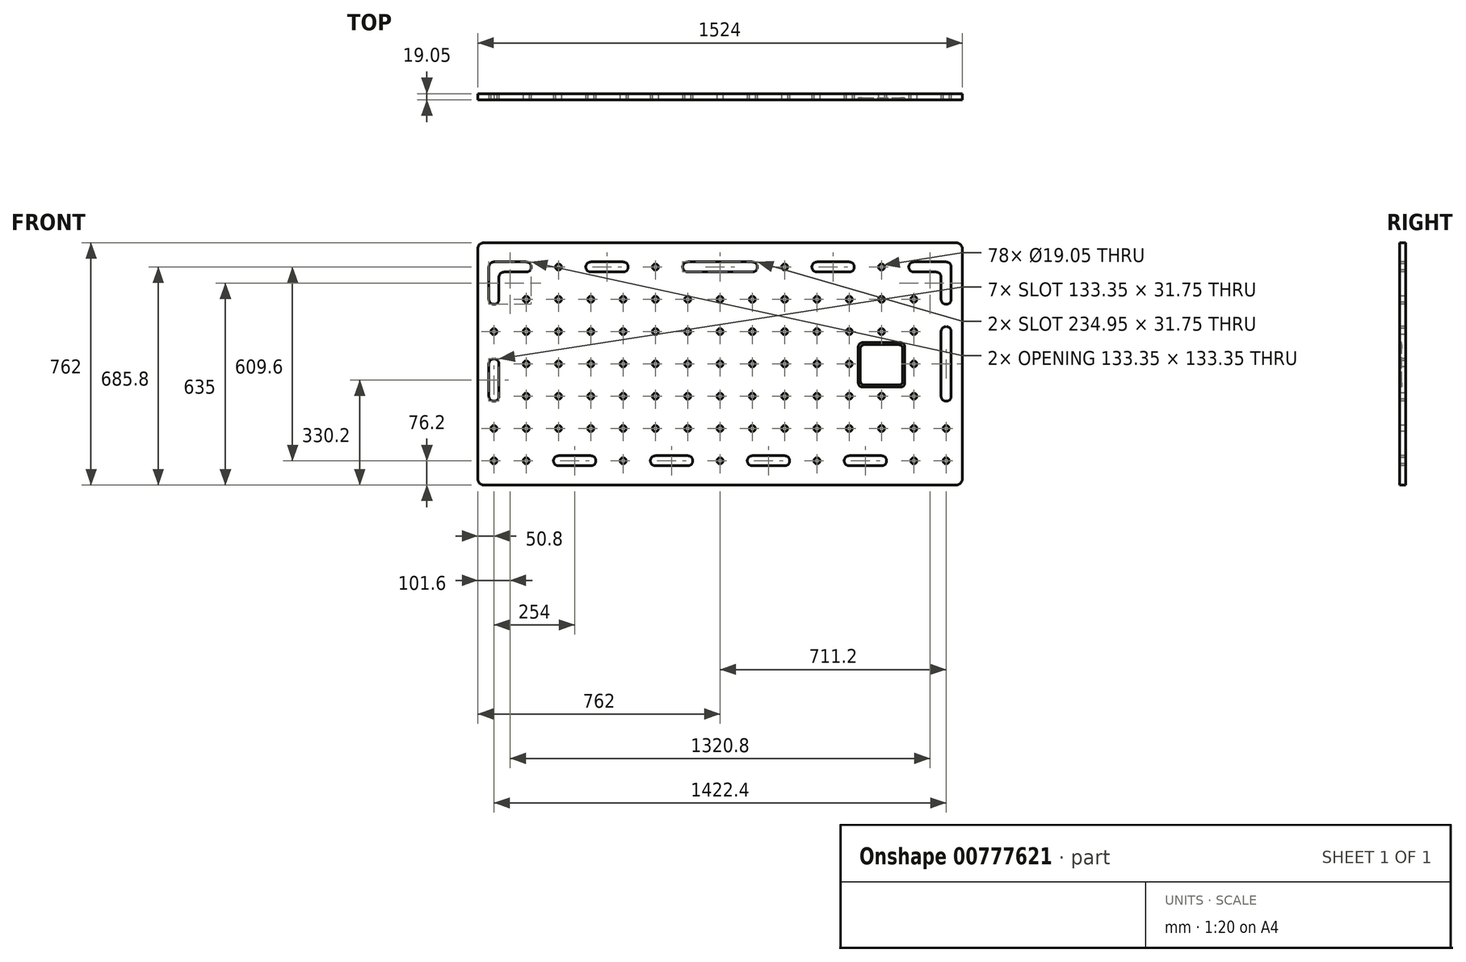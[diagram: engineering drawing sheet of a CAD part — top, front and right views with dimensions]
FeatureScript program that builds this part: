
annotation { "Feature Type Name" : "Feature", "Feature Type Description" : "" }
export const myFeature = defineFeature(function(context is Context, id is Id, definition is map)
    precondition{}
    {
        {
            var Q0;
            Q0=qCreatedBy(makeId("Front.planeOp"),FACE);
            var sketch = newSketch(context, id + "F0", { "sketchPlane" : qUnion([Q0])});
            skLineSegment(sketch, "E0.bottom", {"start": v(742.95, 381) * mm, "end": v(-742.95, 381) * mm});
            skLineSegment(sketch, "E0.top", {"start": v(742.95, -381) * mm, "end": v(-742.95, -381) * mm});
            skLineSegment(sketch, "E0.left", {"start": v(762, 361.95) * mm, "end": v(762, -361.95) * mm});
            skLineSegment(sketch, "E0.right", {"start": v(-762, 361.95) * mm, "end": v(-762, -361.95) * mm});
            skPoint(sketch, "E0.middle", {"position": v(0, 0) * mm});
            skPoint(sketch, "E1.visualSharp", {"position": v(-762, 381) * mm});
            skArc(sketch, "E1.filletArc", {"start": v(-742.95, 381) * mm, "mid": v(-756.42, 375.42) * mm, "end": v(-762, 361.95) * mm});
            skPoint(sketch, "E2.visualSharp", {"position": v(-762, -381) * mm});
            skArc(sketch, "E2.filletArc", {"start": v(-762, -361.95) * mm, "mid": v(-756.42, -375.42) * mm, "end": v(-742.95, -381) * mm});
            skPoint(sketch, "E3.visualSharp", {"position": v(762, -381) * mm});
            skArc(sketch, "E3.filletArc", {"start": v(742.95, -381) * mm, "mid": v(756.42, -375.42) * mm, "end": v(762, -361.95) * mm});
            skPoint(sketch, "E4.visualSharp", {"position": v(762, 381) * mm});
            skArc(sketch, "E4.filletArc", {"start": v(762, 361.95) * mm, "mid": v(756.42, 375.42) * mm, "end": v(742.95, 381) * mm});
            skSolve(sketch);
        }
        {
            var Q0;
            Q0=makeQuery(id+"F0.imprint","IMPRINT",FACE,{"disambiguationData":[TD([[makeQuery(id+"F0.imprint","IMPRINT",EDGE,{"derivedFrom":sQuery(id+"F0.wireOp",EDGE,"E0.bottom")}),1.0]])]});
            extrude(context, id + "F1", {"entities" : qUnion([Q0]), "flatOperationType" : FlatOperationType.REMOVE, "depth" : 19.05 * mm, "offsetDistance" : 25.4 * mm, "domain" : OperationDomain.MODEL});
        }
        {
            var Q0;
            Q0=makeQuery(id+"F1.opExtrude","CAP_FACE",FACE,{"disambiguationData":[OSD([sQuery(id+"F0.wireOp",EDGE,"E0.bottom"),sQuery(id+"F0.wireOp",EDGE,"E0.top"),sQuery(id+"F0.wireOp",EDGE,"E0.left"),sQuery(id+"F0.wireOp",EDGE,"E0.right"),sQuery(id+"F0.wireOp",EDGE,"E1.filletArc"),sQuery(id+"F0.wireOp",EDGE,"E2.filletArc"),sQuery(id+"F0.wireOp",EDGE,"E3.filletArc"),sQuery(id+"F0.wireOp",EDGE,"E4.filletArc")])],"isStart":false});
            var sketch = newSketch(context, id + "F2", { "sketchPlane" : qUnion([Q0]), "disableImprinting" : false});
            skCircle(sketch, "E5", {"center": v(711.2, -304.8) * mm, "radius": 9.53 * mm});
            skCircle(sketch, "E6.0.1.0", {"center": v(711.2, -203.2) * mm, "radius": 9.53 * mm});
            skCircle(sketch, "E6.1.0.0", {"center": v(609.6, -304.8) * mm, "radius": 9.53 * mm});
            skCircle(sketch, "E6.1.1.0", {"center": v(609.6, -203.2) * mm, "radius": 9.53 * mm});
            skCircle(sketch, "E6.1.2.0", {"center": v(609.6, -101.6) * mm, "radius": 9.53 * mm});
            skCircle(sketch, "E6.1.3.0", {"center": v(609.6, 0) * mm, "radius": 9.53 * mm});
            skCircle(sketch, "E6.1.4.0", {"center": v(609.6, 101.6) * mm, "radius": 9.53 * mm});
            skCircle(sketch, "E6.1.5.0", {"center": v(609.6, 203.2) * mm, "radius": 9.53 * mm});
            skCircle(sketch, "E6.2.1.0", {"center": v(508, -203.2) * mm, "radius": 9.53 * mm});
            skCircle(sketch, "E6.2.2.0", {"center": v(508, -101.6) * mm, "radius": 9.53 * mm});
            skCircle(sketch, "E6.2.4.0", {"center": v(508, 101.6) * mm, "radius": 9.53 * mm});
            skCircle(sketch, "E6.2.5.0", {"center": v(508, 203.2) * mm, "radius": 9.53 * mm});
            skCircle(sketch, "E6.2.6.0", {"center": v(508, 304.8) * mm, "radius": 9.53 * mm});
            skCircle(sketch, "E6.3.1.0", {"center": v(406.4, -203.2) * mm, "radius": 9.53 * mm});
            skCircle(sketch, "E6.3.2.0", {"center": v(406.4, -101.6) * mm, "radius": 9.53 * mm});
            skCircle(sketch, "E6.3.3.0", {"center": v(406.4, 0) * mm, "radius": 9.53 * mm});
            skCircle(sketch, "E6.3.4.0", {"center": v(406.4, 101.6) * mm, "radius": 9.53 * mm});
            skCircle(sketch, "E6.3.5.0", {"center": v(406.4, 203.2) * mm, "radius": 9.53 * mm});
            skCircle(sketch, "E6.4.0.0", {"center": v(304.8, -304.8) * mm, "radius": 9.53 * mm});
            skCircle(sketch, "E6.4.1.0", {"center": v(304.8, -203.2) * mm, "radius": 9.53 * mm});
            skCircle(sketch, "E6.4.2.0", {"center": v(304.8, -101.6) * mm, "radius": 9.53 * mm});
            skCircle(sketch, "E6.4.3.0", {"center": v(304.8, 0) * mm, "radius": 9.53 * mm});
            skCircle(sketch, "E6.4.4.0", {"center": v(304.8, 101.6) * mm, "radius": 9.53 * mm});
            skCircle(sketch, "E6.4.5.0", {"center": v(304.8, 203.2) * mm, "radius": 9.53 * mm});
            skCircle(sketch, "E6.5.1.0", {"center": v(203.2, -203.2) * mm, "radius": 9.53 * mm});
            skCircle(sketch, "E6.5.2.0", {"center": v(203.2, -101.6) * mm, "radius": 9.53 * mm});
            skCircle(sketch, "E6.5.3.0", {"center": v(203.2, 0) * mm, "radius": 9.53 * mm});
            skCircle(sketch, "E6.5.4.0", {"center": v(203.2, 101.6) * mm, "radius": 9.53 * mm});
            skCircle(sketch, "E6.5.5.0", {"center": v(203.2, 203.2) * mm, "radius": 9.53 * mm});
            skCircle(sketch, "E6.5.6.0", {"center": v(203.2, 304.8) * mm, "radius": 9.53 * mm});
            skCircle(sketch, "E6.6.1.0", {"center": v(101.6, -203.2) * mm, "radius": 9.53 * mm});
            skCircle(sketch, "E6.6.2.0", {"center": v(101.6, -101.6) * mm, "radius": 9.53 * mm});
            skCircle(sketch, "E6.6.3.0", {"center": v(101.6, 0) * mm, "radius": 9.53 * mm});
            skCircle(sketch, "E6.6.4.0", {"center": v(101.6, 101.6) * mm, "radius": 9.53 * mm});
            skCircle(sketch, "E6.6.5.0", {"center": v(101.6, 203.2) * mm, "radius": 9.53 * mm});
            skCircle(sketch, "E6.7.0.0", {"center": v(0, -304.8) * mm, "radius": 9.53 * mm});
            skCircle(sketch, "E6.7.1.0", {"center": v(0, -203.2) * mm, "radius": 9.53 * mm});
            skCircle(sketch, "E6.7.2.0", {"center": v(0, -101.6) * mm, "radius": 9.53 * mm});
            skCircle(sketch, "E6.7.3.0", {"center": v(0, 0) * mm, "radius": 9.53 * mm});
            skCircle(sketch, "E6.7.4.0", {"center": v(0, 101.6) * mm, "radius": 9.53 * mm});
            skCircle(sketch, "E6.7.5.0", {"center": v(0, 203.2) * mm, "radius": 9.53 * mm});
            skCircle(sketch, "E6.8.1.0", {"center": v(-101.6, -203.2) * mm, "radius": 9.53 * mm});
            skCircle(sketch, "E6.8.2.0", {"center": v(-101.6, -101.6) * mm, "radius": 9.53 * mm});
            skCircle(sketch, "E6.8.3.0", {"center": v(-101.6, 0) * mm, "radius": 9.53 * mm});
            skCircle(sketch, "E6.8.4.0", {"center": v(-101.6, 101.6) * mm, "radius": 9.53 * mm});
            skCircle(sketch, "E6.8.5.0", {"center": v(-101.6, 203.2) * mm, "radius": 9.53 * mm});
            skCircle(sketch, "E6.9.1.0", {"center": v(-203.2, -203.2) * mm, "radius": 9.53 * mm});
            skCircle(sketch, "E6.9.2.0", {"center": v(-203.2, -101.6) * mm, "radius": 9.53 * mm});
            skCircle(sketch, "E6.9.3.0", {"center": v(-203.2, 0) * mm, "radius": 9.53 * mm});
            skCircle(sketch, "E6.9.4.0", {"center": v(-203.2, 101.6) * mm, "radius": 9.53 * mm});
            skCircle(sketch, "E6.9.5.0", {"center": v(-203.2, 203.2) * mm, "radius": 9.53 * mm});
            skCircle(sketch, "E6.9.6.0", {"center": v(-203.2, 304.8) * mm, "radius": 9.53 * mm});
            skCircle(sketch, "E6.10.0.0", {"center": v(-304.8, -304.8) * mm, "radius": 9.53 * mm});
            skCircle(sketch, "E6.10.1.0", {"center": v(-304.8, -203.2) * mm, "radius": 9.53 * mm});
            skCircle(sketch, "E6.10.2.0", {"center": v(-304.8, -101.6) * mm, "radius": 9.53 * mm});
            skCircle(sketch, "E6.10.3.0", {"center": v(-304.8, 0) * mm, "radius": 9.53 * mm});
            skCircle(sketch, "E6.10.4.0", {"center": v(-304.8, 101.6) * mm, "radius": 9.53 * mm});
            skCircle(sketch, "E6.10.5.0", {"center": v(-304.8, 203.2) * mm, "radius": 9.53 * mm});
            skCircle(sketch, "E6.11.1.0", {"center": v(-406.4, -203.2) * mm, "radius": 9.53 * mm});
            skCircle(sketch, "E6.11.2.0", {"center": v(-406.4, -101.6) * mm, "radius": 9.53 * mm});
            skCircle(sketch, "E6.11.3.0", {"center": v(-406.4, 0) * mm, "radius": 9.53 * mm});
            skCircle(sketch, "E6.11.4.0", {"center": v(-406.4, 101.6) * mm, "radius": 9.53 * mm});
            skCircle(sketch, "E6.11.5.0", {"center": v(-406.4, 203.2) * mm, "radius": 9.53 * mm});
            skCircle(sketch, "E6.12.1.0", {"center": v(-508, -203.2) * mm, "radius": 9.53 * mm});
            skCircle(sketch, "E6.12.2.0", {"center": v(-508, -101.6) * mm, "radius": 9.53 * mm});
            skCircle(sketch, "E6.12.3.0", {"center": v(-508, 0) * mm, "radius": 9.53 * mm});
            skCircle(sketch, "E6.12.4.0", {"center": v(-508, 101.6) * mm, "radius": 9.53 * mm});
            skCircle(sketch, "E6.12.5.0", {"center": v(-508, 203.2) * mm, "radius": 9.53 * mm});
            skCircle(sketch, "E6.12.6.0", {"center": v(-508, 304.8) * mm, "radius": 9.53 * mm});
            skCircle(sketch, "E6.13.0.0", {"center": v(-609.6, -304.8) * mm, "radius": 9.53 * mm});
            skCircle(sketch, "E6.13.1.0", {"center": v(-609.6, -203.2) * mm, "radius": 9.53 * mm});
            skCircle(sketch, "E6.13.2.0", {"center": v(-609.6, -101.6) * mm, "radius": 9.53 * mm});
            skCircle(sketch, "E6.13.3.0", {"center": v(-609.6, 0) * mm, "radius": 9.53 * mm});
            skCircle(sketch, "E6.13.4.0", {"center": v(-609.6, 101.6) * mm, "radius": 9.53 * mm});
            skCircle(sketch, "E6.13.5.0", {"center": v(-609.6, 203.2) * mm, "radius": 9.53 * mm});
            skCircle(sketch, "E6.14.0.0", {"center": v(-711.2, -304.8) * mm, "radius": 9.53 * mm});
            skCircle(sketch, "E6.14.1.0", {"center": v(-711.2, -203.2) * mm, "radius": 9.53 * mm});
            skCircle(sketch, "E6.14.4.0", {"center": v(-711.2, 101.6) * mm, "radius": 9.53 * mm});
            skLineSegment(sketch, "E7.bottom", {"start": v(447.75, -72.95) * mm, "end": v(568.4, -72.95) * mm});
            skLineSegment(sketch, "E7.top", {"start": v(447.75, 66.75) * mm, "end": v(568.4, 66.75) * mm});
            skLineSegment(sketch, "E7.left", {"start": v(435.05, -60.25) * mm, "end": v(435.05, 54.05) * mm});
            skLineSegment(sketch, "E7.right", {"start": v(581.1, -60.25) * mm, "end": v(581.1, 54.05) * mm});
            skArc(sketch, "E8.filletArc", {"start": v(447.75, 66.75) * mm, "mid": v(438.76, 63.03) * mm, "end": v(435.05, 54.05) * mm});
            skArc(sketch, "E9.filletArc", {"start": v(581.1, 54.05) * mm, "mid": v(577.38, 63.03) * mm, "end": v(568.4, 66.75) * mm});
            skArc(sketch, "E10.filletArc", {"start": v(568.4, -72.95) * mm, "mid": v(577.38, -69.24) * mm, "end": v(581.1, -60.25) * mm});
            skArc(sketch, "E11.filletArc", {"start": v(435.05, -60.25) * mm, "mid": v(438.76, -69.24) * mm, "end": v(447.75, -72.95) * mm});
            skLineSegment(sketch, "E12.0", {"start": v(454.1, 60.4) * mm, "end": v(562.05, 60.4) * mm});
            skLineSegment(sketch, "E12.1", {"start": v(441.4, -53.9) * mm, "end": v(441.4, 47.7) * mm});
            skLineSegment(sketch, "E12.2", {"start": v(454.1, -66.6) * mm, "end": v(562.05, -66.6) * mm});
            skLineSegment(sketch, "E12.3", {"start": v(574.75, -53.9) * mm, "end": v(574.75, 47.7) * mm});
            skArc(sketch, "E13.filletArc", {"start": v(574.75, 47.7) * mm, "mid": v(571.03, 56.68) * mm, "end": v(562.05, 60.4) * mm});
            skArc(sketch, "E14.filletArc", {"start": v(562.05, -66.6) * mm, "mid": v(571.03, -62.89) * mm, "end": v(574.75, -53.9) * mm});
            skArc(sketch, "E15.filletArc", {"start": v(441.4, -53.9) * mm, "mid": v(445.11, -62.89) * mm, "end": v(454.1, -66.6) * mm});
            skArc(sketch, "E16.filletArc", {"start": v(454.1, 60.4) * mm, "mid": v(445.11, 56.68) * mm, "end": v(441.4, 47.7) * mm});
            skLineSegment(sketch, "E17", {"start": v(-775.52, 0) * mm, "end": v(799.36, 0) * mm, "construction": true});
            skArc(sketch, "E18", {"start": v(-508, -288.92) * mm, "mid": v(-523.88, -304.8) * mm, "end": v(-508, -320.67) * mm});
            skArc(sketch, "E19", {"start": v(-406.4, -320.67) * mm, "mid": v(-390.53, -304.8) * mm, "end": v(-406.4, -288.92) * mm});
            skLineSegment(sketch, "E20", {"start": v(-508, -288.92) * mm, "end": v(-406.4, -288.92) * mm});
            skLineSegment(sketch, "E21", {"start": v(-406.4, -320.67) * mm, "end": v(-508, -320.67) * mm});
            skArc(sketch, "E22", {"start": v(-203.2, -288.92) * mm, "mid": v(-219.08, -304.8) * mm, "end": v(-203.2, -320.67) * mm});
            skArc(sketch, "E23", {"start": v(-101.6, -320.67) * mm, "mid": v(-85.73, -304.8) * mm, "end": v(-101.6, -288.92) * mm});
            skLineSegment(sketch, "E24", {"start": v(-203.2, -288.92) * mm, "end": v(-101.6, -288.92) * mm});
            skLineSegment(sketch, "E25", {"start": v(-101.6, -320.67) * mm, "end": v(-203.2, -320.67) * mm});
            skArc(sketch, "E26", {"start": v(-727.08, -101.6) * mm, "mid": v(-711.2, -117.48) * mm, "end": v(-695.33, -101.6) * mm});
            skArc(sketch, "E27", {"start": v(-695.33, 0) * mm, "mid": v(-711.2, 15.87) * mm, "end": v(-727.08, 0) * mm});
            skLineSegment(sketch, "E28", {"start": v(-695.33, 0) * mm, "end": v(-695.33, -101.6) * mm});
            skLineSegment(sketch, "E29", {"start": v(-727.08, 0) * mm, "end": v(-727.08, -101.6) * mm});
            skArc(sketch, "E30", {"start": v(-727.08, 203.2) * mm, "mid": v(-711.2, 187.32) * mm, "end": v(-695.33, 203.2) * mm});
            skArc(sketch, "E31", {"start": v(-711.04, 320.67) * mm, "mid": v(-722.37, 316.08) * mm, "end": v(-727.08, 304.8) * mm});
            skArc(sketch, "E32", {"start": v(-609.6, 288.92) * mm, "mid": v(-593.73, 304.8) * mm, "end": v(-609.6, 320.67) * mm});
            skLineSegment(sketch, "E33", {"start": v(-711.04, 320.67) * mm, "end": v(-609.6, 320.67) * mm});
            skLineSegment(sketch, "E34", {"start": v(-679.45, 288.92) * mm, "end": v(-609.6, 288.92) * mm});
            skLineSegment(sketch, "E35", {"start": v(-695.33, 273.05) * mm, "end": v(-695.33, 203.2) * mm});
            skLineSegment(sketch, "E36", {"start": v(-727.08, 203.2) * mm, "end": v(-727.08, 304.8) * mm});
            skArc(sketch, "E37", {"start": v(-101.6, 320.67) * mm, "mid": v(-117.48, 304.8) * mm, "end": v(-101.6, 288.92) * mm});
            skArc(sketch, "E38", {"start": v(101.6, 288.92) * mm, "mid": v(117.48, 304.8) * mm, "end": v(101.6, 320.67) * mm});
            skLineSegment(sketch, "E39", {"start": v(-101.6, 320.67) * mm, "end": v(101.6, 320.67) * mm});
            skLineSegment(sketch, "E40", {"start": v(101.6, 288.92) * mm, "end": v(-101.6, 288.92) * mm});
            skArc(sketch, "E41", {"start": v(-406.4, 320.67) * mm, "mid": v(-422.28, 304.8) * mm, "end": v(-406.4, 288.92) * mm});
            skArc(sketch, "E42", {"start": v(-304.8, 288.92) * mm, "mid": v(-288.93, 304.8) * mm, "end": v(-304.8, 320.67) * mm});
            skLineSegment(sketch, "E43", {"start": v(-406.4, 320.67) * mm, "end": v(-304.8, 320.67) * mm});
            skLineSegment(sketch, "E44", {"start": v(-406.4, 288.92) * mm, "end": v(-304.8, 288.92) * mm});
            skArc(sketch, "E45", {"start": v(727.08, 101.6) * mm, "mid": v(711.2, 117.47) * mm, "end": v(695.33, 101.6) * mm});
            skArc(sketch, "E46", {"start": v(695.33, -101.6) * mm, "mid": v(711.2, -117.48) * mm, "end": v(727.08, -101.6) * mm});
            skLineSegment(sketch, "E47", {"start": v(727.08, 101.6) * mm, "end": v(727.08, -101.6) * mm});
            skLineSegment(sketch, "E48", {"start": v(695.33, -101.6) * mm, "end": v(695.33, 101.6) * mm});
            skArc(sketch, "E49", {"start": v(101.6, -288.92) * mm, "mid": v(85.73, -304.8) * mm, "end": v(101.6, -320.67) * mm});
            skArc(sketch, "E50", {"start": v(203.2, -320.67) * mm, "mid": v(219.08, -304.8) * mm, "end": v(203.2, -288.92) * mm});
            skLineSegment(sketch, "E51", {"start": v(101.6, -288.92) * mm, "end": v(203.2, -288.92) * mm});
            skLineSegment(sketch, "E52", {"start": v(203.2, -320.67) * mm, "end": v(101.6, -320.67) * mm});
            skArc(sketch, "E53", {"start": v(508, -320.67) * mm, "mid": v(523.88, -304.8) * mm, "end": v(508, -288.92) * mm});
            skArc(sketch, "E54", {"start": v(406.4, -288.92) * mm, "mid": v(390.53, -304.8) * mm, "end": v(406.4, -320.67) * mm});
            skLineSegment(sketch, "E55", {"start": v(406.4, -320.67) * mm, "end": v(508, -320.67) * mm});
            skLineSegment(sketch, "E56", {"start": v(508, -288.92) * mm, "end": v(406.4, -288.92) * mm});
            skPoint(sketch, "E57.visualSharp", {"position": v(-695.33, 288.92) * mm});
            skArc(sketch, "E57.filletArc", {"start": v(-679.45, 288.92) * mm, "mid": v(-690.68, 284.28) * mm, "end": v(-695.33, 273.05) * mm});
            skArc(sketch, "E58", {"start": v(304.8, 320.67) * mm, "mid": v(288.93, 304.8) * mm, "end": v(304.8, 288.92) * mm});
            skArc(sketch, "E59", {"start": v(406.4, 288.92) * mm, "mid": v(422.28, 304.8) * mm, "end": v(406.4, 320.67) * mm});
            skLineSegment(sketch, "E60", {"start": v(304.8, 288.92) * mm, "end": v(406.4, 288.92) * mm});
            skLineSegment(sketch, "E61", {"start": v(406.4, 320.67) * mm, "end": v(304.8, 320.67) * mm});
            skArc(sketch, "E62", {"start": v(609.6, 320.67) * mm, "mid": v(593.73, 304.8) * mm, "end": v(609.6, 288.92) * mm});
            skArc(sketch, "E63", {"start": v(727.08, 304.8) * mm, "mid": v(722.43, 316.03) * mm, "end": v(711.2, 320.67) * mm});
            skArc(sketch, "E64", {"start": v(695.33, 203.2) * mm, "mid": v(711.2, 187.32) * mm, "end": v(727.08, 203.2) * mm});
            skLineSegment(sketch, "E65", {"start": v(609.6, 288.92) * mm, "end": v(679.45, 288.92) * mm});
            skLineSegment(sketch, "E66", {"start": v(711.2, 320.67) * mm, "end": v(609.6, 320.67) * mm});
            skLineSegment(sketch, "E67", {"start": v(695.33, 203.2) * mm, "end": v(695.33, 273.05) * mm});
            skLineSegment(sketch, "E68", {"start": v(727.08, 304.8) * mm, "end": v(727.08, 203.2) * mm});
            skArc(sketch, "E69.filletArc", {"start": v(695.33, 273.05) * mm, "mid": v(690.68, 284.28) * mm, "end": v(679.45, 288.92) * mm});
            skSolve(sketch);
        }
        {
            var Q0;
            Q0=makeQuery(id+"F2.imprint","IMPRINT",FACE,{"disambiguationData":[TD([[makeQuery(id+"F2.imprint","IMPRINT",EDGE,{"derivedFrom":sQuery(id+"F2.wireOp",EDGE,"E7.bottom")}),1.0]])]});
            extrude(context, id + "F3", {"entities" : qUnion([Q0]), "operationType" : NewBodyOperationType.REMOVE, "oppositeDirection" : true, "depth" : 6.35 * mm, "offsetDistance" : 25.4 * mm});
        }
        {
            var Q0;
            Q0=makeQuery(id+"F2.imprint","IMPRINT",FACE,{"disambiguationData":[TD([[makeQuery(id+"F2.imprint","IMPRINT",EDGE,{"derivedFrom":sQuery(id+"F2.wireOp",EDGE,"E6.14.6.0")}),1.0]])]});
            var Q1;
            Q1=makeQuery(id+"F2.imprint","IMPRINT",FACE,{"disambiguationData":[TD([[makeQuery(id+"F2.imprint","IMPRINT",EDGE,{"derivedFrom":sQuery(id+"F2.wireOp",EDGE,"E6.13.6.0")}),1.0]])]});
            var Q2;
            Q2=makeQuery(id+"F2.imprint","IMPRINT",FACE,{"disambiguationData":[TD([[makeQuery(id+"F2.imprint","IMPRINT",EDGE,{"derivedFrom":sQuery(id+"F2.wireOp",EDGE,"E6.12.6.0")}),1.0]])]});
            var Q3;
            Q3=makeQuery(id+"F2.imprint","IMPRINT",FACE,{"disambiguationData":[TD([[makeQuery(id+"F2.imprint","IMPRINT",EDGE,{"derivedFrom":sQuery(id+"F2.wireOp",EDGE,"E6.12.5.0")}),1.0]])]});
            var Q4;
            Q4=makeQuery(id+"F2.imprint","IMPRINT",FACE,{"disambiguationData":[TD([[makeQuery(id+"F2.imprint","IMPRINT",EDGE,{"derivedFrom":sQuery(id+"F2.wireOp",EDGE,"E6.13.5.0")}),1.0]])]});
            var Q5;
            Q5=makeQuery(id+"F2.imprint","IMPRINT",FACE,{"disambiguationData":[TD([[makeQuery(id+"F2.imprint","IMPRINT",EDGE,{"derivedFrom":sQuery(id+"F2.wireOp",EDGE,"E6.14.5.0")}),1.0]])]});
            var Q6;
            Q6=makeQuery(id+"F2.imprint","IMPRINT",FACE,{"disambiguationData":[TD([[makeQuery(id+"F2.imprint","IMPRINT",EDGE,{"derivedFrom":sQuery(id+"F2.wireOp",EDGE,"E6.14.4.0")}),1.0]])]});
            var Q7;
            Q7=makeQuery(id+"F2.imprint","IMPRINT",FACE,{"disambiguationData":[TD([[makeQuery(id+"F2.imprint","IMPRINT",EDGE,{"derivedFrom":sQuery(id+"F2.wireOp",EDGE,"E6.13.4.0")}),1.0]])]});
            var Q8;
            Q8=makeQuery(id+"F2.imprint","IMPRINT",FACE,{"disambiguationData":[TD([[makeQuery(id+"F2.imprint","IMPRINT",EDGE,{"derivedFrom":sQuery(id+"F2.wireOp",EDGE,"E6.12.4.0")}),1.0]])]});
            var Q9;
            Q9=makeQuery(id+"F2.imprint","IMPRINT",FACE,{"disambiguationData":[TD([[makeQuery(id+"F2.imprint","IMPRINT",EDGE,{"derivedFrom":sQuery(id+"F2.wireOp",EDGE,"E6.12.3.0")}),1.0]])]});
            var Q10;
            Q10=makeQuery(id+"F2.imprint","IMPRINT",FACE,{"disambiguationData":[TD([[makeQuery(id+"F2.imprint","IMPRINT",EDGE,{"derivedFrom":sQuery(id+"F2.wireOp",EDGE,"E6.13.3.0")}),1.0]])]});
            var Q11;
            Q11=makeQuery(id+"F2.imprint","IMPRINT",FACE,{"disambiguationData":[TD([[makeQuery(id+"F2.imprint","IMPRINT",EDGE,{"derivedFrom":sQuery(id+"F2.wireOp",EDGE,"E6.14.3.0")}),1.0]])]});
            var Q12;
            Q12=makeQuery(id+"F2.imprint","IMPRINT",FACE,{"disambiguationData":[TD([[makeQuery(id+"F2.imprint","IMPRINT",EDGE,{"derivedFrom":sQuery(id+"F2.wireOp",EDGE,"E6.14.2.0")}),1.0]])]});
            var Q13;
            Q13=makeQuery(id+"F2.imprint","IMPRINT",FACE,{"disambiguationData":[TD([[makeQuery(id+"F2.imprint","IMPRINT",EDGE,{"derivedFrom":sQuery(id+"F2.wireOp",EDGE,"E6.13.2.0")}),1.0]])]});
            var Q14;
            Q14=makeQuery(id+"F2.imprint","IMPRINT",FACE,{"disambiguationData":[TD([[makeQuery(id+"F2.imprint","IMPRINT",EDGE,{"derivedFrom":sQuery(id+"F2.wireOp",EDGE,"E6.12.2.0")}),1.0]])]});
            var Q15;
            Q15=makeQuery(id+"F2.imprint","IMPRINT",FACE,{"disambiguationData":[TD([[makeQuery(id+"F2.imprint","IMPRINT",EDGE,{"derivedFrom":sQuery(id+"F2.wireOp",EDGE,"E6.12.1.0")}),1.0]])]});
            var Q16;
            Q16=makeQuery(id+"F2.imprint","IMPRINT",FACE,{"disambiguationData":[TD([[makeQuery(id+"F2.imprint","IMPRINT",EDGE,{"derivedFrom":sQuery(id+"F2.wireOp",EDGE,"E6.13.1.0")}),1.0]])]});
            var Q17;
            Q17=makeQuery(id+"F2.imprint","IMPRINT",FACE,{"disambiguationData":[TD([[makeQuery(id+"F2.imprint","IMPRINT",EDGE,{"derivedFrom":sQuery(id+"F2.wireOp",EDGE,"E6.14.1.0")}),1.0]])]});
            var Q18;
            Q18=makeQuery(id+"F2.imprint","IMPRINT",FACE,{"disambiguationData":[TD([[makeQuery(id+"F2.imprint","IMPRINT",EDGE,{"derivedFrom":sQuery(id+"F2.wireOp",EDGE,"E6.14.0.0")}),1.0]])]});
            var Q19;
            Q19=makeQuery(id+"F2.imprint","IMPRINT",FACE,{"disambiguationData":[TD([[makeQuery(id+"F2.imprint","IMPRINT",EDGE,{"derivedFrom":sQuery(id+"F2.wireOp",EDGE,"E6.13.0.0")}),1.0]])]});
            var Q20;
            Q20=makeQuery(id+"F2.imprint","IMPRINT",FACE,{"disambiguationData":[TD([[makeQuery(id+"F2.imprint","IMPRINT",EDGE,{"derivedFrom":sQuery(id+"F2.wireOp",EDGE,"E6.12.0.0")}),1.0]])]});
            var Q21;
            Q21=makeQuery(id+"F2.imprint","IMPRINT",FACE,{"disambiguationData":[TD([[makeQuery(id+"F2.imprint","IMPRINT",EDGE,{"derivedFrom":sQuery(id+"F2.wireOp",EDGE,"E6.11.0.0")}),1.0]])]});
            var Q22;
            Q22=makeQuery(id+"F2.imprint","IMPRINT",FACE,{"disambiguationData":[TD([[makeQuery(id+"F2.imprint","IMPRINT",EDGE,{"derivedFrom":sQuery(id+"F2.wireOp",EDGE,"E6.10.0.0")}),1.0]])]});
            var Q23;
            Q23=makeQuery(id+"F2.imprint","IMPRINT",FACE,{"disambiguationData":[TD([[makeQuery(id+"F2.imprint","IMPRINT",EDGE,{"derivedFrom":sQuery(id+"F2.wireOp",EDGE,"E6.9.0.0")}),1.0]])]});
            var Q24;
            Q24=makeQuery(id+"F2.imprint","IMPRINT",FACE,{"disambiguationData":[TD([[makeQuery(id+"F2.imprint","IMPRINT",EDGE,{"derivedFrom":sQuery(id+"F2.wireOp",EDGE,"E6.9.1.0")}),1.0]])]});
            var Q25;
            Q25=makeQuery(id+"F2.imprint","IMPRINT",FACE,{"disambiguationData":[TD([[makeQuery(id+"F2.imprint","IMPRINT",EDGE,{"derivedFrom":sQuery(id+"F2.wireOp",EDGE,"E6.10.1.0")}),1.0]])]});
            var Q26;
            Q26=makeQuery(id+"F2.imprint","IMPRINT",FACE,{"disambiguationData":[TD([[makeQuery(id+"F2.imprint","IMPRINT",EDGE,{"derivedFrom":sQuery(id+"F2.wireOp",EDGE,"E6.11.1.0")}),1.0]])]});
            var Q27;
            Q27=makeQuery(id+"F2.imprint","IMPRINT",FACE,{"disambiguationData":[TD([[makeQuery(id+"F2.imprint","IMPRINT",EDGE,{"derivedFrom":sQuery(id+"F2.wireOp",EDGE,"E6.11.2.0")}),1.0]])]});
            var Q28;
            Q28=makeQuery(id+"F2.imprint","IMPRINT",FACE,{"disambiguationData":[TD([[makeQuery(id+"F2.imprint","IMPRINT",EDGE,{"derivedFrom":sQuery(id+"F2.wireOp",EDGE,"E6.10.2.0")}),1.0]])]});
            var Q29;
            Q29=makeQuery(id+"F2.imprint","IMPRINT",FACE,{"disambiguationData":[TD([[makeQuery(id+"F2.imprint","IMPRINT",EDGE,{"derivedFrom":sQuery(id+"F2.wireOp",EDGE,"E6.9.2.0")}),1.0]])]});
            var Q30;
            Q30=makeQuery(id+"F2.imprint","IMPRINT",FACE,{"disambiguationData":[TD([[makeQuery(id+"F2.imprint","IMPRINT",EDGE,{"derivedFrom":sQuery(id+"F2.wireOp",EDGE,"E6.9.3.0")}),1.0]])]});
            var Q31;
            Q31=makeQuery(id+"F2.imprint","IMPRINT",FACE,{"disambiguationData":[TD([[makeQuery(id+"F2.imprint","IMPRINT",EDGE,{"derivedFrom":sQuery(id+"F2.wireOp",EDGE,"E6.10.3.0")}),1.0]])]});
            var Q32;
            Q32=makeQuery(id+"F2.imprint","IMPRINT",FACE,{"disambiguationData":[TD([[makeQuery(id+"F2.imprint","IMPRINT",EDGE,{"derivedFrom":sQuery(id+"F2.wireOp",EDGE,"E6.11.3.0")}),1.0]])]});
            var Q33;
            Q33=makeQuery(id+"F2.imprint","IMPRINT",FACE,{"disambiguationData":[TD([[makeQuery(id+"F2.imprint","IMPRINT",EDGE,{"derivedFrom":sQuery(id+"F2.wireOp",EDGE,"E6.11.4.0")}),1.0]])]});
            var Q34;
            Q34=makeQuery(id+"F2.imprint","IMPRINT",FACE,{"disambiguationData":[TD([[makeQuery(id+"F2.imprint","IMPRINT",EDGE,{"derivedFrom":sQuery(id+"F2.wireOp",EDGE,"E6.10.4.0")}),1.0]])]});
            var Q35;
            Q35=makeQuery(id+"F2.imprint","IMPRINT",FACE,{"disambiguationData":[TD([[makeQuery(id+"F2.imprint","IMPRINT",EDGE,{"derivedFrom":sQuery(id+"F2.wireOp",EDGE,"E6.9.4.0")}),1.0]])]});
            var Q36;
            Q36=makeQuery(id+"F2.imprint","IMPRINT",FACE,{"disambiguationData":[TD([[makeQuery(id+"F2.imprint","IMPRINT",EDGE,{"derivedFrom":sQuery(id+"F2.wireOp",EDGE,"E6.9.5.0")}),1.0]])]});
            var Q37;
            Q37=makeQuery(id+"F2.imprint","IMPRINT",FACE,{"disambiguationData":[TD([[makeQuery(id+"F2.imprint","IMPRINT",EDGE,{"derivedFrom":sQuery(id+"F2.wireOp",EDGE,"E6.10.5.0")}),1.0]])]});
            var Q38;
            Q38=makeQuery(id+"F2.imprint","IMPRINT",FACE,{"disambiguationData":[TD([[makeQuery(id+"F2.imprint","IMPRINT",EDGE,{"derivedFrom":sQuery(id+"F2.wireOp",EDGE,"E6.11.5.0")}),1.0]])]});
            var Q39;
            Q39=makeQuery(id+"F2.imprint","IMPRINT",FACE,{"disambiguationData":[TD([[makeQuery(id+"F2.imprint","IMPRINT",EDGE,{"derivedFrom":sQuery(id+"F2.wireOp",EDGE,"E6.11.6.0")}),1.0]])]});
            var Q40;
            Q40=makeQuery(id+"F2.imprint","IMPRINT",FACE,{"disambiguationData":[TD([[makeQuery(id+"F2.imprint","IMPRINT",EDGE,{"derivedFrom":sQuery(id+"F2.wireOp",EDGE,"E6.10.6.0")}),1.0]])]});
            var Q41;
            Q41=makeQuery(id+"F2.imprint","IMPRINT",FACE,{"disambiguationData":[TD([[makeQuery(id+"F2.imprint","IMPRINT",EDGE,{"derivedFrom":sQuery(id+"F2.wireOp",EDGE,"E6.9.6.0")}),1.0]])]});
            var Q42;
            Q42=makeQuery(id+"F2.imprint","IMPRINT",FACE,{"disambiguationData":[TD([[makeQuery(id+"F2.imprint","IMPRINT",EDGE,{"derivedFrom":sQuery(id+"F2.wireOp",EDGE,"E6.8.6.0")}),1.0]])]});
            var Q43;
            Q43=makeQuery(id+"F2.imprint","IMPRINT",FACE,{"disambiguationData":[TD([[makeQuery(id+"F2.imprint","IMPRINT",EDGE,{"derivedFrom":sQuery(id+"F2.wireOp",EDGE,"E6.7.6.0")}),1.0]])]});
            var Q44;
            Q44=makeQuery(id+"F2.imprint","IMPRINT",FACE,{"disambiguationData":[TD([[makeQuery(id+"F2.imprint","IMPRINT",EDGE,{"derivedFrom":sQuery(id+"F2.wireOp",EDGE,"E6.6.6.0")}),1.0]])]});
            var Q45;
            Q45=makeQuery(id+"F2.imprint","IMPRINT",FACE,{"disambiguationData":[TD([[makeQuery(id+"F2.imprint","IMPRINT",EDGE,{"derivedFrom":sQuery(id+"F2.wireOp",EDGE,"E6.6.5.0")}),1.0]])]});
            var Q46;
            Q46=makeQuery(id+"F2.imprint","IMPRINT",FACE,{"disambiguationData":[TD([[makeQuery(id+"F2.imprint","IMPRINT",EDGE,{"derivedFrom":sQuery(id+"F2.wireOp",EDGE,"E6.7.5.0")}),1.0]])]});
            var Q47;
            Q47=makeQuery(id+"F2.imprint","IMPRINT",FACE,{"disambiguationData":[TD([[makeQuery(id+"F2.imprint","IMPRINT",EDGE,{"derivedFrom":sQuery(id+"F2.wireOp",EDGE,"E6.8.5.0")}),1.0]])]});
            var Q48;
            Q48=makeQuery(id+"F2.imprint","IMPRINT",FACE,{"disambiguationData":[TD([[makeQuery(id+"F2.imprint","IMPRINT",EDGE,{"derivedFrom":sQuery(id+"F2.wireOp",EDGE,"E6.8.4.0")}),1.0]])]});
            var Q49;
            Q49=makeQuery(id+"F2.imprint","IMPRINT",FACE,{"disambiguationData":[TD([[makeQuery(id+"F2.imprint","IMPRINT",EDGE,{"derivedFrom":sQuery(id+"F2.wireOp",EDGE,"E6.7.4.0")}),1.0]])]});
            var Q50;
            Q50=makeQuery(id+"F2.imprint","IMPRINT",FACE,{"disambiguationData":[TD([[makeQuery(id+"F2.imprint","IMPRINT",EDGE,{"derivedFrom":sQuery(id+"F2.wireOp",EDGE,"E6.6.4.0")}),1.0]])]});
            var Q51;
            Q51=makeQuery(id+"F2.imprint","IMPRINT",FACE,{"disambiguationData":[TD([[makeQuery(id+"F2.imprint","IMPRINT",EDGE,{"derivedFrom":sQuery(id+"F2.wireOp",EDGE,"E6.6.3.0")}),1.0]])]});
            var Q52;
            Q52=makeQuery(id+"F2.imprint","IMPRINT",FACE,{"disambiguationData":[TD([[makeQuery(id+"F2.imprint","IMPRINT",EDGE,{"derivedFrom":sQuery(id+"F2.wireOp",EDGE,"E6.7.3.0")}),1.0]])]});
            var Q53;
            Q53=makeQuery(id+"F2.imprint","IMPRINT",FACE,{"disambiguationData":[TD([[makeQuery(id+"F2.imprint","IMPRINT",EDGE,{"derivedFrom":sQuery(id+"F2.wireOp",EDGE,"E6.8.3.0")}),1.0]])]});
            var Q54;
            Q54=makeQuery(id+"F2.imprint","IMPRINT",FACE,{"disambiguationData":[TD([[makeQuery(id+"F2.imprint","IMPRINT",EDGE,{"derivedFrom":sQuery(id+"F2.wireOp",EDGE,"E6.8.2.0")}),1.0]])]});
            var Q55;
            Q55=makeQuery(id+"F2.imprint","IMPRINT",FACE,{"disambiguationData":[TD([[makeQuery(id+"F2.imprint","IMPRINT",EDGE,{"derivedFrom":sQuery(id+"F2.wireOp",EDGE,"E6.7.2.0")}),1.0]])]});
            var Q56;
            Q56=makeQuery(id+"F2.imprint","IMPRINT",FACE,{"disambiguationData":[TD([[makeQuery(id+"F2.imprint","IMPRINT",EDGE,{"derivedFrom":sQuery(id+"F2.wireOp",EDGE,"E6.6.2.0")}),1.0]])]});
            var Q57;
            Q57=makeQuery(id+"F2.imprint","IMPRINT",FACE,{"disambiguationData":[TD([[makeQuery(id+"F2.imprint","IMPRINT",EDGE,{"derivedFrom":sQuery(id+"F2.wireOp",EDGE,"E6.6.1.0")}),1.0]])]});
            var Q58;
            Q58=makeQuery(id+"F2.imprint","IMPRINT",FACE,{"disambiguationData":[TD([[makeQuery(id+"F2.imprint","IMPRINT",EDGE,{"derivedFrom":sQuery(id+"F2.wireOp",EDGE,"E6.7.1.0")}),1.0]])]});
            var Q59;
            Q59=makeQuery(id+"F2.imprint","IMPRINT",FACE,{"disambiguationData":[TD([[makeQuery(id+"F2.imprint","IMPRINT",EDGE,{"derivedFrom":sQuery(id+"F2.wireOp",EDGE,"E6.8.1.0")}),1.0]])]});
            var Q60;
            Q60=makeQuery(id+"F2.imprint","IMPRINT",FACE,{"disambiguationData":[TD([[makeQuery(id+"F2.imprint","IMPRINT",EDGE,{"derivedFrom":sQuery(id+"F2.wireOp",EDGE,"E6.8.0.0")}),1.0]])]});
            var Q61;
            Q61=makeQuery(id+"F2.imprint","IMPRINT",FACE,{"disambiguationData":[TD([[makeQuery(id+"F2.imprint","IMPRINT",EDGE,{"derivedFrom":sQuery(id+"F2.wireOp",EDGE,"E6.7.0.0")}),1.0]])]});
            var Q62;
            Q62=makeQuery(id+"F2.imprint","IMPRINT",FACE,{"disambiguationData":[TD([[makeQuery(id+"F2.imprint","IMPRINT",EDGE,{"derivedFrom":sQuery(id+"F2.wireOp",EDGE,"E6.6.0.0")}),1.0]])]});
            var Q63;
            Q63=makeQuery(id+"F2.imprint","IMPRINT",FACE,{"disambiguationData":[TD([[makeQuery(id+"F2.imprint","IMPRINT",EDGE,{"derivedFrom":sQuery(id+"F2.wireOp",EDGE,"E6.5.0.0")}),1.0]])]});
            var Q64;
            Q64=makeQuery(id+"F2.imprint","IMPRINT",FACE,{"disambiguationData":[TD([[makeQuery(id+"F2.imprint","IMPRINT",EDGE,{"derivedFrom":sQuery(id+"F2.wireOp",EDGE,"E6.4.0.0")}),1.0]])]});
            var Q65;
            Q65=makeQuery(id+"F2.imprint","IMPRINT",FACE,{"disambiguationData":[TD([[makeQuery(id+"F2.imprint","IMPRINT",EDGE,{"derivedFrom":sQuery(id+"F2.wireOp",EDGE,"E6.3.0.0")}),1.0]])]});
            var Q66;
            Q66=makeQuery(id+"F2.imprint","IMPRINT",FACE,{"disambiguationData":[TD([[makeQuery(id+"F2.imprint","IMPRINT",EDGE,{"derivedFrom":sQuery(id+"F2.wireOp",EDGE,"E6.3.1.0")}),1.0]])]});
            var Q67;
            Q67=makeQuery(id+"F2.imprint","IMPRINT",FACE,{"disambiguationData":[TD([[makeQuery(id+"F2.imprint","IMPRINT",EDGE,{"derivedFrom":sQuery(id+"F2.wireOp",EDGE,"E6.4.1.0")}),1.0]])]});
            var Q68;
            Q68=makeQuery(id+"F2.imprint","IMPRINT",FACE,{"disambiguationData":[TD([[makeQuery(id+"F2.imprint","IMPRINT",EDGE,{"derivedFrom":sQuery(id+"F2.wireOp",EDGE,"E6.5.1.0")}),1.0]])]});
            var Q69;
            Q69=makeQuery(id+"F2.imprint","IMPRINT",FACE,{"disambiguationData":[TD([[makeQuery(id+"F2.imprint","IMPRINT",EDGE,{"derivedFrom":sQuery(id+"F2.wireOp",EDGE,"E6.5.2.0")}),1.0]])]});
            var Q70;
            Q70=makeQuery(id+"F2.imprint","IMPRINT",FACE,{"disambiguationData":[TD([[makeQuery(id+"F2.imprint","IMPRINT",EDGE,{"derivedFrom":sQuery(id+"F2.wireOp",EDGE,"E6.4.2.0")}),1.0]])]});
            var Q71;
            Q71=makeQuery(id+"F2.imprint","IMPRINT",FACE,{"disambiguationData":[TD([[makeQuery(id+"F2.imprint","IMPRINT",EDGE,{"derivedFrom":sQuery(id+"F2.wireOp",EDGE,"E6.3.2.0")}),1.0]])]});
            var Q72;
            Q72=makeQuery(id+"F2.imprint","IMPRINT",FACE,{"disambiguationData":[TD([[makeQuery(id+"F2.imprint","IMPRINT",EDGE,{"derivedFrom":sQuery(id+"F2.wireOp",EDGE,"E6.3.3.0")}),1.0]])]});
            var Q73;
            Q73=makeQuery(id+"F2.imprint","IMPRINT",FACE,{"disambiguationData":[TD([[makeQuery(id+"F2.imprint","IMPRINT",EDGE,{"derivedFrom":sQuery(id+"F2.wireOp",EDGE,"E6.4.3.0")}),1.0]])]});
            var Q74;
            Q74=makeQuery(id+"F2.imprint","IMPRINT",FACE,{"disambiguationData":[TD([[makeQuery(id+"F2.imprint","IMPRINT",EDGE,{"derivedFrom":sQuery(id+"F2.wireOp",EDGE,"E6.5.3.0")}),1.0]])]});
            var Q75;
            Q75=makeQuery(id+"F2.imprint","IMPRINT",FACE,{"disambiguationData":[TD([[makeQuery(id+"F2.imprint","IMPRINT",EDGE,{"derivedFrom":sQuery(id+"F2.wireOp",EDGE,"E6.5.4.0")}),1.0]])]});
            var Q76;
            Q76=makeQuery(id+"F2.imprint","IMPRINT",FACE,{"disambiguationData":[TD([[makeQuery(id+"F2.imprint","IMPRINT",EDGE,{"derivedFrom":sQuery(id+"F2.wireOp",EDGE,"E6.4.4.0")}),1.0]])]});
            var Q77;
            Q77=makeQuery(id+"F2.imprint","IMPRINT",FACE,{"disambiguationData":[TD([[makeQuery(id+"F2.imprint","IMPRINT",EDGE,{"derivedFrom":sQuery(id+"F2.wireOp",EDGE,"E6.3.4.0")}),1.0]])]});
            var Q78;
            Q78=makeQuery(id+"F2.imprint","IMPRINT",FACE,{"disambiguationData":[TD([[makeQuery(id+"F2.imprint","IMPRINT",EDGE,{"derivedFrom":sQuery(id+"F2.wireOp",EDGE,"E6.3.5.0")}),1.0]])]});
            var Q79;
            Q79=makeQuery(id+"F2.imprint","IMPRINT",FACE,{"disambiguationData":[TD([[makeQuery(id+"F2.imprint","IMPRINT",EDGE,{"derivedFrom":sQuery(id+"F2.wireOp",EDGE,"E6.4.5.0")}),1.0]])]});
            var Q80;
            Q80=makeQuery(id+"F2.imprint","IMPRINT",FACE,{"disambiguationData":[TD([[makeQuery(id+"F2.imprint","IMPRINT",EDGE,{"derivedFrom":sQuery(id+"F2.wireOp",EDGE,"E6.5.5.0")}),1.0]])]});
            var Q81;
            Q81=makeQuery(id+"F2.imprint","IMPRINT",FACE,{"disambiguationData":[TD([[makeQuery(id+"F2.imprint","IMPRINT",EDGE,{"derivedFrom":sQuery(id+"F2.wireOp",EDGE,"E6.5.6.0")}),1.0]])]});
            var Q82;
            Q82=makeQuery(id+"F2.imprint","IMPRINT",FACE,{"disambiguationData":[TD([[makeQuery(id+"F2.imprint","IMPRINT",EDGE,{"derivedFrom":sQuery(id+"F2.wireOp",EDGE,"E6.4.6.0")}),1.0]])]});
            var Q83;
            Q83=makeQuery(id+"F2.imprint","IMPRINT",FACE,{"disambiguationData":[TD([[makeQuery(id+"F2.imprint","IMPRINT",EDGE,{"derivedFrom":sQuery(id+"F2.wireOp",EDGE,"E6.3.6.0")}),1.0]])]});
            var Q84;
            Q84=makeQuery(id+"F2.imprint","IMPRINT",FACE,{"disambiguationData":[TD([[makeQuery(id+"F2.imprint","IMPRINT",EDGE,{"derivedFrom":sQuery(id+"F2.wireOp",EDGE,"E6.2.6.0")}),1.0]])]});
            var Q85;
            Q85=makeQuery(id+"F2.imprint","IMPRINT",FACE,{"disambiguationData":[TD([[makeQuery(id+"F2.imprint","IMPRINT",EDGE,{"derivedFrom":sQuery(id+"F2.wireOp",EDGE,"E6.1.6.0")}),1.0]])]});
            var Q86;
            Q86=makeQuery(id+"F2.imprint","IMPRINT",FACE,{"disambiguationData":[TD([[makeQuery(id+"F2.imprint","IMPRINT",EDGE,{"derivedFrom":sQuery(id+"F2.wireOp",EDGE,"E6.0.6.0")}),1.0]])]});
            var Q87;
            Q87=makeQuery(id+"F2.imprint","IMPRINT",FACE,{"disambiguationData":[TD([[makeQuery(id+"F2.imprint","IMPRINT",EDGE,{"derivedFrom":sQuery(id+"F2.wireOp",EDGE,"E6.0.5.0")}),1.0]])]});
            var Q88;
            Q88=makeQuery(id+"F2.imprint","IMPRINT",FACE,{"disambiguationData":[TD([[makeQuery(id+"F2.imprint","IMPRINT",EDGE,{"derivedFrom":sQuery(id+"F2.wireOp",EDGE,"E6.1.5.0")}),1.0]])]});
            var Q89;
            Q89=makeQuery(id+"F2.imprint","IMPRINT",FACE,{"disambiguationData":[TD([[makeQuery(id+"F2.imprint","IMPRINT",EDGE,{"derivedFrom":sQuery(id+"F2.wireOp",EDGE,"E6.2.5.0")}),1.0]])]});
            var Q90;
            Q90=makeQuery(id+"F2.imprint","IMPRINT",FACE,{"disambiguationData":[TD([[makeQuery(id+"F2.imprint","IMPRINT",EDGE,{"derivedFrom":sQuery(id+"F2.wireOp",EDGE,"E6.2.4.0")}),1.0]])]});
            var Q91;
            Q91=makeQuery(id+"F2.imprint","IMPRINT",FACE,{"disambiguationData":[TD([[makeQuery(id+"F2.imprint","IMPRINT",EDGE,{"derivedFrom":sQuery(id+"F2.wireOp",EDGE,"E6.1.4.0")}),1.0]])]});
            var Q92;
            Q92=makeQuery(id+"F2.imprint","IMPRINT",FACE,{"disambiguationData":[TD([[makeQuery(id+"F2.imprint","IMPRINT",EDGE,{"derivedFrom":sQuery(id+"F2.wireOp",EDGE,"E6.0.4.0")}),1.0]])]});
            var Q93;
            Q93=makeQuery(id+"F2.imprint","IMPRINT",FACE,{"disambiguationData":[TD([[makeQuery(id+"F2.imprint","IMPRINT",EDGE,{"derivedFrom":sQuery(id+"F2.wireOp",EDGE,"E6.0.3.0")}),1.0]])]});
            var Q94;
            Q94=makeQuery(id+"F2.imprint","IMPRINT",FACE,{"disambiguationData":[TD([[makeQuery(id+"F2.imprint","IMPRINT",EDGE,{"derivedFrom":sQuery(id+"F2.wireOp",EDGE,"E6.1.3.0")}),1.0]])]});
            var Q95;
            Q95=makeQuery(id+"F2.imprint","IMPRINT",FACE,{"disambiguationData":[TD([[makeQuery(id+"F2.imprint","IMPRINT",EDGE,{"derivedFrom":sQuery(id+"F2.wireOp",EDGE,"E6.2.2.0")}),1.0]])]});
            var Q96;
            Q96=makeQuery(id+"F2.imprint","IMPRINT",FACE,{"disambiguationData":[TD([[makeQuery(id+"F2.imprint","IMPRINT",EDGE,{"derivedFrom":sQuery(id+"F2.wireOp",EDGE,"E6.1.2.0")}),1.0]])]});
            var Q97;
            Q97=makeQuery(id+"F2.imprint","IMPRINT",FACE,{"disambiguationData":[TD([[makeQuery(id+"F2.imprint","IMPRINT",EDGE,{"derivedFrom":sQuery(id+"F2.wireOp",EDGE,"E6.0.2.0")}),1.0]])]});
            var Q98;
            Q98=makeQuery(id+"F2.imprint","IMPRINT",FACE,{"disambiguationData":[TD([[makeQuery(id+"F2.imprint","IMPRINT",EDGE,{"derivedFrom":sQuery(id+"F2.wireOp",EDGE,"E6.2.1.0")}),1.0]])]});
            var Q99;
            Q99=makeQuery(id+"F2.imprint","IMPRINT",FACE,{"disambiguationData":[TD([[makeQuery(id+"F2.imprint","IMPRINT",EDGE,{"derivedFrom":sQuery(id+"F2.wireOp",EDGE,"E6.1.1.0")}),1.0]])]});
            var Q100;
            Q100=makeQuery(id+"F2.imprint","IMPRINT",FACE,{"disambiguationData":[TD([[makeQuery(id+"F2.imprint","IMPRINT",EDGE,{"derivedFrom":sQuery(id+"F2.wireOp",EDGE,"E6.0.1.0")}),1.0]])]});
            var Q101;
            Q101=makeQuery(id+"F2.imprint","IMPRINT",FACE,{"disambiguationData":[TD([[makeQuery(id+"F2.imprint","IMPRINT",EDGE,{"derivedFrom":sQuery(id+"F2.wireOp",EDGE,"E5")}),1.0]])]});
            var Q102;
            Q102=makeQuery(id+"F2.imprint","IMPRINT",FACE,{"disambiguationData":[TD([[makeQuery(id+"F2.imprint","IMPRINT",EDGE,{"derivedFrom":sQuery(id+"F2.wireOp",EDGE,"E6.1.0.0")}),1.0]])]});
            var Q103;
            Q103=makeQuery(id+"F2.imprint","IMPRINT",FACE,{"disambiguationData":[TD([[makeQuery(id+"F2.imprint","IMPRINT",EDGE,{"derivedFrom":sQuery(id+"F2.wireOp",EDGE,"E6.2.0.0")}),1.0]])]});
            extrude(context, id + "F4", {"entities" : qUnion([Q0, Q1, Q2, Q3, Q4, Q5, Q6, Q7, Q8, Q9, Q10, Q11, Q12, Q13, Q14, Q15, Q16, Q17, Q18, Q19, Q20, Q21, Q22, Q23, Q24, Q25, Q26, Q27, Q28, Q29, Q30, Q31, Q32, Q33, Q34, Q35, Q36, Q37, Q38, Q39, Q40, Q41, Q42, Q43, Q44, Q45, Q46, Q47, Q48, Q49, Q50, Q51, Q52, Q53, Q54, Q55, Q56, Q57, Q58, Q59, Q60, Q61, Q62, Q63, Q64, Q65, Q66, Q67, Q68, Q69, Q70, Q71, Q72, Q73, Q74, Q75, Q76, Q77, Q78, Q79, Q80, Q81, Q82, Q83, Q84, Q85, Q86, Q87, Q88, Q89, Q90, Q91, Q92, Q93, Q94, Q95, Q96, Q97, Q98, Q99, Q100, Q101, Q102, Q103]), "operationType" : NewBodyOperationType.REMOVE, "oppositeDirection" : true, "depth" : 19.05 * mm, "offsetDistance" : 25.4 * mm});
        }
        {
            var Q0;
            Q0=makeQuery(id+"F2.imprint","IMPRINT",FACE,{"disambiguationData":[TD([[makeQuery(id+"F2.imprint","IMPRINT",EDGE,{"derivedFrom":sQuery(id+"F2.wireOp",EDGE,"E18")}),1.0]])]});
            var Q1;
            Q1=makeQuery(id+"F2.imprint","IMPRINT",FACE,{"disambiguationData":[TD([[makeQuery(id+"F2.imprint","IMPRINT",EDGE,{"derivedFrom":sQuery(id+"F2.wireOp",EDGE,"E22")}),1.0]])]});
            var Q2;
            Q2=makeQuery(id+"F2.imprint","IMPRINT",FACE,{"disambiguationData":[TD([[makeQuery(id+"F2.imprint","IMPRINT",EDGE,{"derivedFrom":sQuery(id+"F2.wireOp",EDGE,"E49")}),1.0]])]});
            var Q3;
            Q3=makeQuery(id+"F2.imprint","IMPRINT",FACE,{"disambiguationData":[TD([[makeQuery(id+"F2.imprint","IMPRINT",EDGE,{"derivedFrom":sQuery(id+"F2.wireOp",EDGE,"E53")}),1.0]])]});
            var Q4;
            Q4=makeQuery(id+"F2.imprint","IMPRINT",FACE,{"disambiguationData":[TD([[makeQuery(id+"F2.imprint","IMPRINT",EDGE,{"derivedFrom":sQuery(id+"F2.wireOp",EDGE,"E45")}),1.0]])]});
            var Q5;
            Q5=makeQuery(id+"F2.imprint","IMPRINT",FACE,{"disambiguationData":[TD([[makeQuery(id+"F2.imprint","IMPRINT",EDGE,{"derivedFrom":sQuery(id+"F2.wireOp",EDGE,"E62")}),1.0]])]});
            var Q6;
            Q6=makeQuery(id+"F2.imprint","IMPRINT",FACE,{"disambiguationData":[TD([[makeQuery(id+"F2.imprint","IMPRINT",EDGE,{"derivedFrom":sQuery(id+"F2.wireOp",EDGE,"E58")}),1.0]])]});
            var Q7;
            Q7=makeQuery(id+"F2.imprint","IMPRINT",FACE,{"disambiguationData":[TD([[makeQuery(id+"F2.imprint","IMPRINT",EDGE,{"derivedFrom":sQuery(id+"F2.wireOp",EDGE,"E37")}),1.0]])]});
            var Q8;
            Q8=makeQuery(id+"F2.imprint","IMPRINT",FACE,{"disambiguationData":[TD([[makeQuery(id+"F2.imprint","IMPRINT",EDGE,{"derivedFrom":sQuery(id+"F2.wireOp",EDGE,"E41")}),1.0]])]});
            var Q9;
            Q9=makeQuery(id+"F2.imprint","IMPRINT",FACE,{"disambiguationData":[TD([[makeQuery(id+"F2.imprint","IMPRINT",EDGE,{"derivedFrom":sQuery(id+"F2.wireOp",EDGE,"E30")}),1.0]])]});
            var Q10;
            Q10=makeQuery(id+"F2.imprint","IMPRINT",FACE,{"disambiguationData":[TD([[makeQuery(id+"F2.imprint","IMPRINT",EDGE,{"derivedFrom":sQuery(id+"F2.wireOp",EDGE,"E26")}),1.0]])]});
            extrude(context, id + "F5", {"entities" : qUnion([Q0, Q1, Q2, Q3, Q4, Q5, Q6, Q7, Q8, Q9, Q10]), "operationType" : NewBodyOperationType.REMOVE, "oppositeDirection" : true, "depth" : 19.05 * mm, "offsetDistance" : 25.4 * mm});
        }
    });
